# Revit family: Shower_Trim-DXV-Oak-Hill_D35155540_Series
name_source: partatom
category: Plumbing Fixtures
units: mm (PartAtom-declared; Revit-internal decimal feet)

## family parameters
Cut with Voids When Loaded = No
Host = Face
OmniClass Number = 23.45.05.14.17
OmniClass Title = Showers
Part Type = Normal
Room Calculation Point = No
Round Connector Dimension = Use Diameter
Shared = Yes

## types (8) — shared parameters
Assembly Code = D2010710
CW Connection = Yes
CWFU = 3
Cold Water Connection Diameter = 1/2"
Cold Water Connection Radius = 1/4"
Default Elevation = 48"
Description = Pressure Balance Shower Valve Trim with D35101SS10.191 Shower Rough Valve
HW Connection = Yes
HWFU = 3
Height = 8"
Hot Water Connection Diameter = 1/2"
Hot Water Connection Radius = 1/4"
Installation Type = Wall Mount
Manufacturer = DXV
Price = Prices may vary. Please consult Manufacturer Representative for most up-to-date price list.
Tempered Water Connection = Yes
Tempered Water Connection Diameter = 1/2"
Tempered Water Connection Radius = 1/4"
URL = https://www.dxv.com
Vent Connection = No
WFU = 4
Waste Connection = No
Width = 8"

## per-type parameters (varying)
| type | Finish | Material | Model | Rough Valve Distance | Standard Installation | Thin-Wall Installation |
| D35155540.100 (Standard Installation) | Cast Brass-DXV-100-Polished Chrome | Cast Brass-DXV-100-Polished Chrome | D35155540.100 | 2 5/16" | Yes | No |
| D35155540.100 (Thin-Wall Installation) | Cast Brass-DXV-100-Polished Chrome | Cast Brass-DXV-100-Polished Chrome | D35155540.100 | 1" | No | Yes |
| D35155540.144 (Standard Installation) | Cast Brass-DXV-144-Brushed Nickel | Cast Brass-DXV-144-Brushed Nickel | D35155540.144 | 2 5/16" | Yes | No |
| D35155540.150 (Standard Installation) | Cast Brass-DXV-150-Platinum Nickel | Cast Brass-DXV-150-Platinum Nickel | D35155540.150 | 2 5/16" | Yes | No |
| D35155540.427 (Standard Installation) | Cast Brass-DXV-427-Satin Brass | Cast Brass-DXV-427-Satin Brass | D35155540.427 | 2 5/16" | Yes | No |
| D35155540.144 (Thin-Wall Installation) | Cast Brass-DXV-144-Brushed Nickel | Cast Brass-DXV-144-Brushed Nickel | D35155540.144 | 1" | No | Yes |
| D35155540.150 (Thin-Wall Installation) | Cast Brass-DXV-150-Platinum Nickel | Cast Brass-DXV-150-Platinum Nickel | D35155540.150 | 1" | No | Yes |
| D35155540.427 (Thin-Wall Installation) | Cast Brass-DXV-427-Satin Brass | Cast Brass-DXV-427-Satin Brass | D35155540.427 | 1" | No | Yes |

## geometry (parser evidence)
native form markers: Sweep x2
no freeform markers — native parametric forms only
